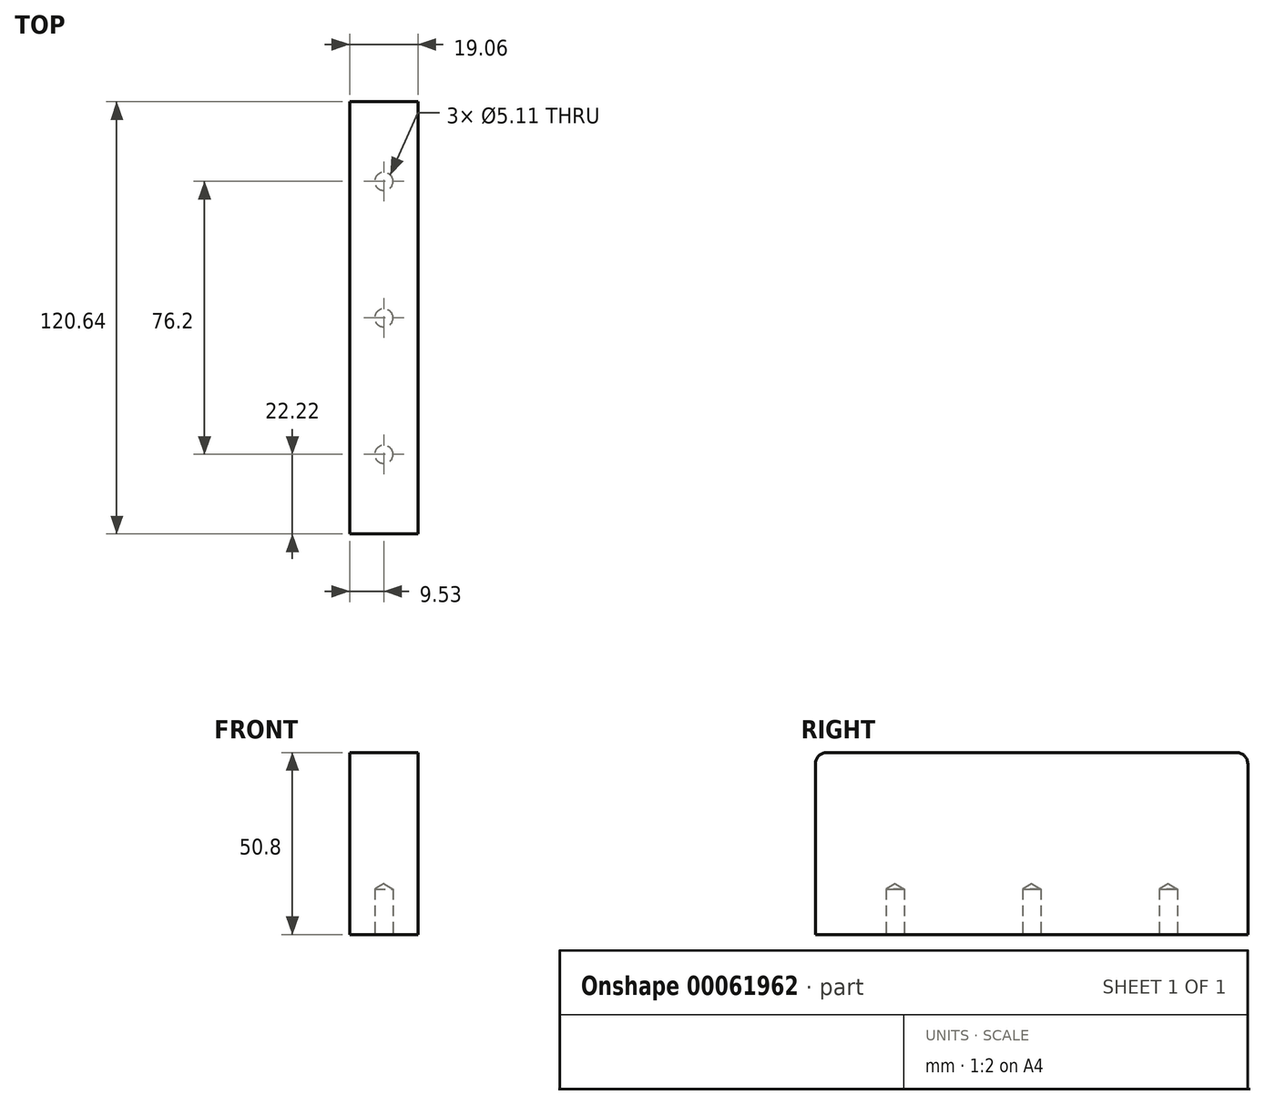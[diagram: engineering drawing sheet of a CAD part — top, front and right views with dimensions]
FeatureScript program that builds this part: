
annotation { "Feature Type Name" : "Feature", "Feature Type Description" : "" }
export const myFeature = defineFeature(function(context is Context, id is Id, definition is map)
    precondition{}
    {
        {
            var Q0;
            Q0=qCreatedBy(makeId("Right.planeOp"),FACE);
            var sketch = newSketch(context, id + "F0", { "sketchPlane" : qUnion([Q0])});
            skLineSegment(sketch, "E0.rect.bottom", {"start": v(-60.32, -25.4) * mm, "end": v(60.33, -25.4) * mm});
            skLineSegment(sketch, "E0.rect.top", {"start": v(-60.33, 25.4) * mm, "end": v(60.32, 25.4) * mm});
            skLineSegment(sketch, "E0.rect.left", {"start": v(-60.32, -25.4) * mm, "end": v(-60.33, 25.4) * mm});
            skLineSegment(sketch, "E0.rect.right", {"start": v(60.33, -25.4) * mm, "end": v(60.32, 25.4) * mm});
            skPoint(sketch, "E0.rect.middle", {"position": v(0, 0) * mm});
            skSolve(sketch);
        }
        {
            var Q0;
            Q0 = qSketchRegion(id + "F0", true);
            extrude(context, id + "F1", {"entities" : qUnion([Q0]), "endBound" : BoundingType.SYMMETRIC, "depth" : 19.05 * mm});
        }
        {
            var Q0;
            Q0=makeQuery(id+"F1.opExtrude","SWEPT_EDGE",EDGE,{"disambiguationData":[OSD([sQuery(id+"F0.wireOp",EDGE,"E0.rect.top"),sQuery(id+"F0.wireOp",EDGE,"E0.rect.left")])]});
            var Q1;
            Q1=makeQuery(id+"F1.opExtrude","SWEPT_EDGE",EDGE,{"disambiguationData":[OSD([sQuery(id+"F0.wireOp",EDGE,"E0.rect.top"),sQuery(id+"F0.wireOp",EDGE,"E0.rect.right")])]});
            fillet(context, id + "F2", {"entities" : qUnion([Q0, Q1]), "radius" : 3.17 * mm, "tangentPropagation" : true, "allowEdgeOverflow" : false});
        }
        {
            var Q0;
            Q0=makeQuery(id+"F1.opExtrude","SWEPT_FACE",FACE,{"disambiguationData":[OSD([sQuery(id+"F0.wireOp",EDGE,"E0.rect.bottom")])]});
            var sketch = newSketch(context, id + "F3", { "sketchPlane" : qUnion([Q0])});
            skPoint(sketch, "E1", {"position": v(0, 38.1) * mm});
            skPoint(sketch, "E2", {"position": v(0, 0) * mm});
            skPoint(sketch, "E3", {"position": v(0, -38.1) * mm});
            skLineSegment(sketch, "E4", {"start": v(0, 38.1) * mm, "end": v(0, 0) * mm, "construction": true});
            skLineSegment(sketch, "E5", {"start": v(0, -38.1) * mm, "end": v(0, 0) * mm, "construction": true});
            skLineSegment(sketch, "E6", {"start": v(9.53, 0) * mm, "end": v(-9.53, 0) * mm});
            skSolve(sketch);
        }
        {
            var Q0;
            Q0=sQuery(id+"F3.wireOp",VERTEX,"E1");
            var Q1;
            Q1=sQuery(id+"F3.wireOp",VERTEX,"E2");
            var Q2;
            Q2=sQuery(id+"F3.wireOp",VERTEX,"E3");
            var Q3;
            Q3=makeQuery(id+"F1.opExtrude","SWEPT_BODY",BODY,{"disambiguationData":[OSD([sQuery(id+"F0.wireOp",EDGE,"E0.rect.bottom"),sQuery(id+"F0.wireOp",EDGE,"E0.rect.top"),sQuery(id+"F0.wireOp",EDGE,"E0.rect.left"),sQuery(id+"F0.wireOp",EDGE,"E0.rect.right")])]});
            hole(context, id + "F4", {"style" : HoleStyle.SIMPLE, "holeDiameter" : 5.1 * mm, "endStyle" : HoleEndStyle.BLIND, "holeDepth" : 12.7 * mm, "locations" : qUnion([Q0, Q1, Q2]), "scope" : qUnion([Q3]), "standardTappedOrClearance" : lookupTablePath({ "fit" : "Normal (ASME)", "standard" : "ANSI", "engagement" : "75%", "pitch" : "20 tpi", "size" : "1/4", "type" : "Tapped" }), "standardBlindInLast" : lookupTablePath({ "fit" : "Free", "standard" : "ANSI", "engagement" : "75%", "pitch" : "20 tpi", "size" : "1/4", "type" : "Tapped" }), "majorDiameter" : 6.35 * mm});
        }
    });
